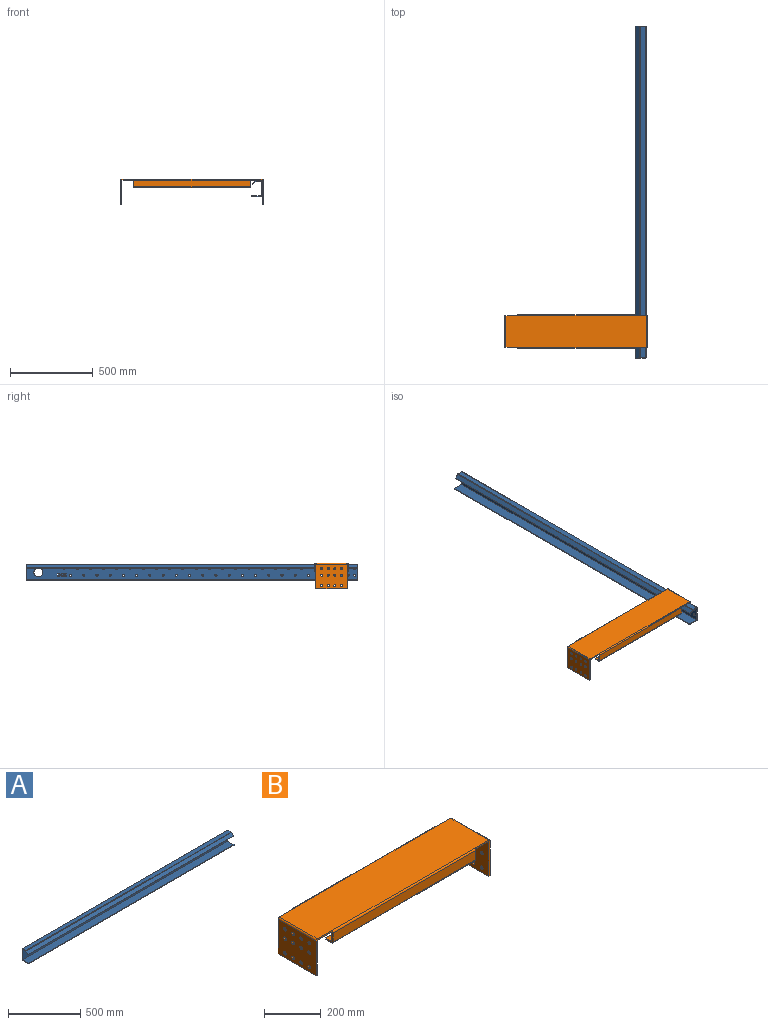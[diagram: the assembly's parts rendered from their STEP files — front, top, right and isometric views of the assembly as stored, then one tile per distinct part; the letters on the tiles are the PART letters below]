
ASSEMBLY  parts=2 mates=1
PART A: 152 faces, bbox 2010x65x99 mm
  f0: plane 59.99x5mm, normal (-1,0,0), area 299.9mm2, adj f2,f3,f4,f149
  f1: plane 59.99x5mm, normal (1,0,0), area 299.9mm2, adj f2,f3,f4,f148
  f2: plane 2010x5mm, normal (0,-1,0), area 10050mm2, adj f0,f1,f3,f4
  f3: plane 2010x59.99mm, normal (0,0,-1), area 120579.9mm2, adj f0,f1,f2,f150
  f4: plane 2010x59.99mm, normal (0,0,1), area 120579.9mm2, adj f0,f1,f2,f151
  f5: plane 5x3.01mm, normal (0,0,-1), area 15.1mm2, adj f6,f128,f129,f130
  f6: plane 9.21x5mm, normal (1,0,0), area 46.1mm2, adj f5,f7,f129,f130
  f7: extruded ~5x2.77mm, area 14.5mm2, adj f6,f8,f129,f130
  f8: extruded ~5x2.04mm, area 13.9mm2, adj f7,f9,f129,f130
  f9: extruded ~5x3.16mm, area 16.2mm2, adj f8,f10,f129,f130
  f10: extruded ~5x4.26mm, area 23mm2, adj f9,f11,f129,f130
  f11: extruded ~5x3.85mm, area 21.3mm2, adj f10,f12,f129,f130
  f12: plane 9.17x5mm, normal (-1,0,0), area 45.9mm2, adj f11,f13,f129,f130
  f13: plane 5x3.01mm, normal (0,0,-1), area 15mm2, adj f12,f14,f129,f130
  f14: plane 8.72x5mm, normal (1,0,0), area 43.6mm2, adj f13,f15,f129,f130
  f15: extruded ~5x2.42mm, area 12.8mm2, adj f14,f16,f129,f130
  f16: extruded ~5x2.19mm, area 12mm2, adj f15,f17,f129,f130
  f17: extruded ~5x2.15mm, area 11.8mm2, adj f16,f18,f129,f130
  f18: extruded ~5x2.43mm, area 12.9mm2, adj f17,f128,f129,f130
  f19: plane 5x2.49mm, normal (-1,0,0), area 12.5mm2, adj f20,f127,f129,f130
  f20: plane 10.22x5mm, normal (0,0,-1), area 51.1mm2, adj f19,f21,f129,f130
  f21: plane 5x1.95mm, normal (1,0,0), area 9.7mm2, adj f20,f22,f129,f130
  f22: plane 9.8x6.82mm, normal (0.82,0,0.57), area 59.7mm2, adj f21,f23,f129,f130
  f23: plane 7x5mm, normal (0,0,-1), area 35mm2, adj f22,f24,f129,f130
  f24: plane 5x2.49mm, normal (1,0,0), area 12.5mm2, adj f23,f25,f129,f130
  f25: plane 10.59x5mm, normal (0,0,1), area 53mm2, adj f24,f26,f129,f130
  f26: plane 5x1.96mm, normal (-1,0,0), area 9.8mm2, adj f25,f27,f129,f130
  f27: plane 9.79x6.83mm, normal (-0.82,0,-0.57), area 59.7mm2, adj f26,f127,f129,f130
  f28: plane 5x3.01mm, normal (0,0,-1), area 15.1mm2, adj f29,f126,f129,f130
  f29: plane 9.21x5mm, normal (1,0,0), area 46.1mm2, adj f28,f30,f129,f130
  f30: extruded ~5x2.77mm, area 14.5mm2, adj f29,f31,f129,f130
  f31: extruded ~5x2.04mm, area 13.9mm2, adj f30,f32,f129,f130
  f32: extruded ~5x3.16mm, area 16.2mm2, adj f31,f33,f129,f130
  f33: extruded ~5x4.26mm, area 23mm2, adj f32,f34,f129,f130
  f34: extruded ~5x3.85mm, area 21.3mm2, adj f33,f35,f129,f130
  f35: plane 9.17x5mm, normal (-1,0,0), area 45.9mm2, adj f34,f36,f129,f130
  f36: plane 5x3.01mm, normal (0,0,-1), area 15mm2, adj f35,f37,f129,f130
  f37: plane 8.72x5mm, normal (1,0,0), area 43.6mm2, adj f36,f38,f129,f130
  f38: extruded ~5x2.42mm, area 12.8mm2, adj f37,f39,f129,f130
  f39: extruded ~5x2.19mm, area 12mm2, adj f38,f40,f129,f130
  f40: extruded ~5x2.15mm, area 11.8mm2, adj f39,f41,f129,f130
  f41: extruded ~5x2.43mm, area 12.9mm2, adj f40,f126,f129,f130
  f42: extruded ~5x2.44mm, area 13mm2, adj f43,f125,f129,f130
  f43: extruded ~5x1.83mm, area 9.3mm2, adj f42,f44,f129,f130
  f44: extruded ~5x1.52mm, area 8mm2, adj f43,f45,f129,f130
  f45: extruded ~5x1.13mm, area 6.5mm2, adj f44,f46,f129,f130
  f46: extruded ~5x0.74mm, area 4mm2, adj f45,f47,f129,f130
  f47: extruded ~5x0.69mm, area 4.7mm2, adj f46,f48,f129,f130
  f48: extruded ~5x1.85mm, area 10.4mm2, adj f47,f49,f129,f130
  f49: extruded ~5x1.32mm, area 7.5mm2, adj f48,f50,f129,f130
  f50: extruded ~5x0.63mm, area 3.9mm2, adj f49,f51,f129,f130
  f51: extruded ~5x1.32mm, area 8.4mm2, adj f50,f52,f129,f130
  f52: extruded ~5x1.75mm, area 9.1mm2, adj f51,f53,f129,f130
  f53: extruded ~5x2.97mm, area 16.7mm2, adj f52,f54,f129,f130
  f54: extruded ~5x3.54mm, area 18.9mm2, adj f53,f55,f129,f130
  f55: extruded ~5x2.12mm, area 10.7mm2, adj f54,f56,f129,f130
  f56: extruded ~5x1.91mm, area 10.1mm2, adj f55,f57,f129,f130
  f57: extruded ~5x0.2mm, area 1.1mm2, adj f56,f58,f129,f130
  f58: plane 5x2.35mm, normal (0.92,0,0.38), area 12.7mm2, adj f57,f59,f129,f130
  f59: extruded ~5x1.89mm, area 10mm2, adj f58,f60,f129,f130
  f60: extruded ~5x1.46mm, area 7.4mm2, adj f59,f61,f129,f130
  f61: extruded ~5x1.32mm, area 7mm2, adj f60,f62,f129,f130
  f62: extruded ~5x1.04mm, area 5.9mm2, adj f61,f63,f129,f130
  f63: extruded ~5x0.7mm, area 3.7mm2, adj f62,f64,f129,f130
  f64: extruded ~5x0.59mm, area 4.1mm2, adj f63,f65,f129,f130
  f65: extruded ~5x1.91mm, area 10.8mm2, adj f64,f66,f129,f130
  f66: extruded ~5x2.2mm, area 13mm2, adj f65,f67,f129,f130
  f67: extruded ~5x0.55mm, area 3.8mm2, adj f66,f68,f129,f130
  f68: extruded ~5x2.35mm, area 12.6mm2, adj f67,f69,f129,f130
  f69: extruded ~5x3.04mm, area 17.3mm2, adj f68,f70,f129,f130
  f70: extruded ~5x3.86mm, area 20.5mm2, adj f69,f71,f129,f130
  f71: extruded ~5x4.03mm, area 20.8mm2, adj f70,f125,f129,f130
  f72: plane 14.24x5mm, normal (1,0,0), area 71.2mm2, adj f73,f124,f129,f130
  f73: plane 5x3.02mm, normal (0,0,1), area 15.1mm2, adj f72,f74,f129,f130
  f74: plane 14.24x5mm, normal (-1,0,0), area 71.2mm2, adj f73,f124,f129,f130
  f75: plane 88.98x5mm, normal (-1,0,0), area 444.9mm2, adj f129,f130,f145,f149
  f76: plane 88.98x5mm, normal (1,0,0), area 444.9mm2, adj f129,f130,f144,f148
  f77: cylinder r=6.5mm len=13mm, axis (0,1,0), area 204.2mm2, adj f129,f130
  f78: cylinder r=6.5mm len=13mm, axis (0,1,0), area 204.2mm2, adj f129,f130
  f79: cylinder r=6.5mm len=13mm, axis (0,1,0), area 204.2mm2, adj f129,f130
  f80: cylinder r=6.5mm len=13mm, axis (0,1,0), area 204.2mm2, adj f129,f130
  f81: cylinder r=6.5mm len=13mm, axis (0,1,0), area 204.2mm2, adj f129,f130
  f82: cylinder r=6.5mm len=13mm, axis (0,1,0), area 204.2mm2, adj f129,f130
  f83: cylinder r=6.5mm len=13mm, axis (0,1,0), area 204.2mm2, adj f129,f130
  f84: cylinder r=6.5mm len=13mm, axis (0,1,0), area 204.2mm2, adj f129,f130
  f85: cylinder r=6.5mm len=13mm, axis (0,1,0), area 204.2mm2, adj f129,f130
  f86: cylinder r=6.5mm len=13mm, axis (0,1,0), area 204.2mm2, adj f129,f130
  f87: cylinder r=6.5mm len=13mm, axis (0,1,0), area 204.2mm2, adj f129,f130
  f88: cylinder r=6.5mm len=13mm, axis (0,1,0), area 204.2mm2, adj f129,f130
  f89: cylinder r=6.5mm len=13mm, axis (0,1,0), area 204.2mm2, adj f129,f130
  f90: cylinder r=6.5mm len=13mm, axis (0,1,0), area 204.2mm2, adj f129,f130
  f91: cylinder r=6.5mm len=13mm, axis (0,1,0), area 204.2mm2, adj f129,f130
  f92: cylinder r=6.5mm len=13mm, axis (0,1,0), area 204.2mm2, adj f129,f130
  f93: cylinder r=6.5mm len=13mm, axis (0,1,0), area 204.2mm2, adj f129,f130
  f94: cylinder r=6.5mm len=13mm, axis (0,1,0), area 204.2mm2, adj f129,f130
  f95: cylinder r=6.5mm len=13mm, axis (0,1,0), area 204.2mm2, adj f129,f130
  f96: cylinder r=6.5mm len=13mm, axis (0,1,0), area 204.2mm2, adj f129,f130
  f97: cylinder r=6.5mm len=13mm, axis (0,1,0), area 204.2mm2, adj f129,f130
  f98: cylinder r=6.5mm len=13mm, axis (0,1,0), area 204.2mm2, adj f129,f130
  f99: cylinder r=6.5mm len=13mm, axis (0,1,0), area 204.2mm2, adj f129,f130
  f100: cylinder r=6.5mm len=13mm, axis (0,1,0), area 204.2mm2, adj f129,f130
  f101: cylinder r=6.5mm len=13mm, axis (0,1,0), area 204.2mm2, adj f129,f130
  f102: cylinder r=6.5mm len=13mm, axis (0,1,0), area 204.2mm2, adj f129,f130
  f103: cylinder r=6.5mm len=13mm, axis (0,1,0), area 204.2mm2, adj f129,f130
  f104: cylinder r=6.5mm len=13mm, axis (0,1,0), area 204.2mm2, adj f129,f130
  f105: cylinder r=6.5mm len=13mm, axis (0,1,0), area 204.2mm2, adj f129,f130
  f106: cylinder r=6.5mm len=13mm, axis (0,1,0), area 204.2mm2, adj f129,f130
  f107: cylinder r=6.5mm len=13mm, axis (0,1,0), area 204.2mm2, adj f129,f130
  f108: cylinder r=6.5mm len=13mm, axis (0,1,0), area 204.2mm2, adj f129,f130
  f109: cylinder r=6.5mm len=13mm, axis (0,1,0), area 204.2mm2, adj f129,f130
  f110: cylinder r=6.5mm len=13mm, axis (0,1,0), area 204.2mm2, adj f129,f130
  f111: cylinder r=6.5mm len=13mm, axis (0,1,0), area 204.2mm2, adj f129,f130
  f112: cylinder r=6.5mm len=13mm, axis (0,1,0), area 204.2mm2, adj f129,f130
  f113: cylinder r=6.5mm len=13mm, axis (0,1,0), area 204.2mm2, adj f129,f130
  f114: cylinder r=6.5mm len=13mm, axis (0,1,0), area 204.2mm2, adj f129,f130
  f115: cylinder r=6.5mm len=13mm, axis (0,1,0), area 204.2mm2, adj f129,f130
  f116: cylinder r=6.5mm len=13mm, axis (0,1,0), area 204.2mm2, adj f129,f130
  f117: cylinder r=27mm len=54mm, axis (0,1,0), area 848.2mm2, adj f129,f130
  f118: cylinder r=6.5mm len=13mm, axis (0,1,0), area 204.2mm2, adj f129,f130
  f119: cylinder r=6.5mm len=13mm, axis (0,1,0), area 204.2mm2, adj f129,f130
  f120: cylinder r=6.5mm len=13mm, axis (0,1,0), area 204.2mm2, adj f129,f130
  f121: cylinder r=6.5mm len=13mm, axis (0,1,0), area 204.2mm2, adj f129,f130
  f122: cylinder r=6.5mm len=13mm, axis (0,1,0), area 204.2mm2, adj f129,f130
  f123: cylinder r=6.5mm len=13mm, axis (0,1,0), area 204.2mm2, adj f129,f130
  f124: plane 5x3.02mm, normal (0,0,-1), area 15.1mm2, adj f72,f74,f129,f130
  f125: plane 5x2.8mm, normal (-1,0,0), area 14mm2, adj f42,f71,f129,f130
  f126: plane 8.7x5mm, normal (-1,0,0), area 43.5mm2, adj f28,f41,f129,f130
  f127: plane 6.64x5mm, normal (0,0,1), area 33.2mm2, adj f19,f27,f129,f130
  f128: plane 8.7x5mm, normal (-1,0,0), area 43.5mm2, adj f5,f18,f129,f130
  f129: plane 2010x88.98mm, normal (0,1,0), area 170067.6mm2, adj f5,f6,f7,f8,f9,f10,f11,f12
  f130: plane 2010x88.98mm, normal (0,-1,0), area 170067.6mm2, adj f5,f6,f7,f8,f9,f10,f11,f12
  f131: plane 31.99x5mm, normal (-1,0,0), area 159.9mm2, adj f133,f134,f141,f145
  f132: plane 31.99x5mm, normal (1,0,0), area 159.9mm2, adj f133,f134,f140,f144
  f133: plane 2010x31.99mm, normal (0,0,1), area 64292mm2, adj f131,f132,f142,f146
  f134: plane 2010x31.99mm, normal (0,0,-1), area 64292mm2, adj f131,f132,f143,f147
  f135: plane 23.87x22.77mm, normal (-1,0,0), area 140mm2, adj f136,f138,f139,f141
  f136: plane 2010x3.65mm, normal (0,-0.73,-0.68), area 10050mm2, adj f135,f137,f138,f139
  f137: plane 23.87x22.77mm, normal (1,0,0), area 140mm2, adj f136,f138,f139,f140
  f138: plane 2010x20.46mm, normal (0,-0.68,0.73), area 56272.1mm2, adj f135,f136,f137,f142
  f139: plane 2010x20.46mm, normal (0,0.68,-0.73), area 56272.1mm2, adj f135,f136,f137,f143
  f140: plane 5x3.42mm, normal (1,0,0), area 9.4mm2, adj f132,f137,f142,f143
  f141: plane 5x3.42mm, normal (-1,0,0), area 9.4mm2, adj f131,f135,f142,f143
  f142: cylinder r=5.01mm len=2010mm, axis (1,0,0), area 7567.5mm2, adj f133,f138,f140,f141
  f143: cylinder r=0.01mm len=2010mm, axis (1,0,0), area 15.1mm2, adj f134,f139,f140,f141
  f144: plane 5.01x5.01mm, normal (1,0,0), area 19.7mm2, adj f76,f132,f146,f147
  f145: plane 5.01x5.01mm, normal (-1,0,0), area 19.7mm2, adj f75,f131,f146,f147
  f146: cylinder r=5.01mm len=2010mm, axis (1,0,0), area 15818.1mm2, adj f129,f133,f144,f145
  f147: cylinder r=0.01mm len=2010mm, axis (1,0,0), area 31.6mm2, adj f130,f134,f144,f145
  f148: plane 5.01x5.01mm, normal (1,0,0), area 19.7mm2, adj f1,f76,f150,f151
  f149: plane 5.01x5.01mm, normal (-1,0,0), area 19.7mm2, adj f0,f75,f150,f151
  f150: cylinder r=5.01mm len=2010mm, axis (1,0,0), area 15818.1mm2, adj f3,f129,f148,f149
  f151: cylinder r=0.01mm len=2010mm, axis (1,0,0), area 31.6mm2, adj f4,f130,f148,f149
PART B: 94 faces, bbox 862x202x156 mm
  f0: plane 70x6mm, normal (0,1,0), area 420mm2, adj f10,f12,f13,f90
  f1: plane 70x6mm, normal (0,-1,0), area 420mm2, adj f7,f12,f13,f73
  f2: plane 6x2.31mm, normal (-1,0,0), area 13.9mm2, adj f8,f12,f13,f56
  f3: plane 6x2.31mm, normal (1,0,0), area 13.9mm2, adj f11,f12,f13,f33
  f4: plane 6x2.31mm, normal (-1,0,0), area 13.9mm2, adj f7,f12,f13,f57
  f5: plane 6x2.31mm, normal (1,0,0), area 13.9mm2, adj f10,f12,f13,f34
  f6: plane 70x6mm, normal (0,-1,0), area 420mm2, adj f11,f12,f13,f74
  f7: plane 6x0.99mm, normal (0,-1,0), area 5.9mm2, adj f1,f4,f12,f13
  f8: plane 6x0.99mm, normal (0,1,0), area 5.9mm2, adj f2,f9,f12,f13
  f9: plane 70x6mm, normal (0,1,0), area 420mm2, adj f8,f12,f13,f91
  f10: plane 6x0.99mm, normal (0,1,0), area 5.9mm2, adj f0,f5,f12,f13
  f11: plane 6x0.99mm, normal (0,-1,0), area 5.9mm2, adj f3,f6,f12,f13
  f12: plane 849.98x189.98mm, normal (0,0,-1), area 161479.2mm2, adj f0,f1,f2,f3,f4,f5,f6,f7
  f13: plane 849.98x189.98mm, normal (0,0,1), area 161479.2mm2, adj f0,f1,f2,f3,f4,f5,f6,f7
  f14: plane 6x2.32mm, normal (0,0,1), area 13.9mm2, adj f30,f31,f32,f34
  f15: plane 190x6mm, normal (0,0,-1), area 1140mm2, adj f16,f30,f31,f32
  f16: plane 149.99x6mm, normal (0,-1,0), area 899.9mm2, adj f15,f17,f31,f32
  f17: plane 6x2.32mm, normal (0,0,1), area 13.9mm2, adj f16,f31,f32,f33
  f18: cylinder r=6.5mm len=13mm, axis (-1,0,0), area 245mm2, adj f31,f32
  f19: cylinder r=6.5mm len=13mm, axis (-1,0,0), area 245mm2, adj f31,f32
  f20: cylinder r=6.5mm len=13mm, axis (-1,0,0), area 245mm2, adj f31,f32
  f21: cylinder r=6.5mm len=13mm, axis (-1,0,0), area 245mm2, adj f31,f32
  f22: cylinder r=6.5mm len=13mm, axis (-1,0,0), area 245mm2, adj f31,f32
  f23: cylinder r=6.5mm len=13mm, axis (-1,0,0), area 245mm2, adj f31,f32
  f24: cylinder r=6.5mm len=13mm, axis (-1,0,0), area 245mm2, adj f31,f32
  f25: cylinder r=6.5mm len=13mm, axis (-1,0,0), area 245mm2, adj f31,f32
  f26: cylinder r=6.5mm len=13mm, axis (-1,0,0), area 245mm2, adj f31,f32
  f27: cylinder r=6.5mm len=13mm, axis (-1,0,0), area 245mm2, adj f31,f32
  f28: cylinder r=6.5mm len=13mm, axis (-1,0,0), area 245mm2, adj f31,f32
  f29: cylinder r=6.5mm len=13mm, axis (-1,0,0), area 245mm2, adj f31,f32
  f30: plane 149.99x6mm, normal (0,1,0), area 899.9mm2, adj f14,f15,f31,f32
  f31: plane 190x149.99mm, normal (-1,0,0), area 26905.3mm2, adj f14,f15,f16,f17,f18,f19,f20,f21
  f32: plane 190x149.99mm, normal (1,0,0), area 26905.3mm2, adj f14,f15,f16,f17,f18,f19,f20,f21
  f33: plane 6.01x6.01mm, normal (0,-1,0), area 28.4mm2, adj f3,f17,f35,f36
  f34: plane 6.01x6.01mm, normal (0,1,0), area 28.4mm2, adj f5,f14,f35,f36
  f35: cylinder r=6.01mm len=185.36mm, axis (0,-1,0), area 1749.9mm2, adj f13,f32,f33,f34
  f36: cylinder r=0.01mm len=185.36mm, axis (0,-1,0), area 2.9mm2, adj f12,f31,f33,f34
  f37: plane 6x2.32mm, normal (0,0,1), area 13.9mm2, adj f53,f54,f55,f57
  f38: plane 190x6mm, normal (0,0,-1), area 1140mm2, adj f39,f53,f54,f55
  f39: plane 149.99x6mm, normal (0,1,0), area 899.9mm2, adj f38,f40,f54,f55
  f40: plane 6x2.32mm, normal (0,0,1), area 13.9mm2, adj f39,f54,f55,f56
  f41: cylinder r=6.5mm len=13mm, axis (1,0,0), area 245mm2, adj f54,f55
  f42: cylinder r=6.5mm len=13mm, axis (1,0,0), area 245mm2, adj f54,f55
  f43: cylinder r=6.5mm len=13mm, axis (1,0,0), area 245mm2, adj f54,f55
  f44: cylinder r=6.5mm len=13mm, axis (1,0,0), area 245mm2, adj f54,f55
  f45: cylinder r=6.5mm len=13mm, axis (1,0,0), area 245mm2, adj f54,f55
  f46: cylinder r=6.5mm len=13mm, axis (1,0,0), area 245mm2, adj f54,f55
  f47: cylinder r=6.5mm len=13mm, axis (1,0,0), area 245mm2, adj f54,f55
  f48: cylinder r=6.5mm len=13mm, axis (1,0,0), area 245mm2, adj f54,f55
  f49: cylinder r=6.5mm len=13mm, axis (1,0,0), area 245mm2, adj f54,f55
  f50: cylinder r=6.5mm len=13mm, axis (1,0,0), area 245mm2, adj f54,f55
  f51: cylinder r=6.5mm len=13mm, axis (1,0,0), area 245mm2, adj f54,f55
  f52: cylinder r=6.5mm len=13mm, axis (1,0,0), area 245mm2, adj f54,f55
  f53: plane 149.99x6mm, normal (0,-1,0), area 899.9mm2, adj f37,f38,f54,f55
  f54: plane 190x149.99mm, normal (1,0,0), area 26905.3mm2, adj f37,f38,f39,f40,f41,f42,f43,f44
  f55: plane 190x149.99mm, normal (-1,0,0), area 26905.3mm2, adj f37,f38,f39,f40,f41,f42,f43,f44
  f56: plane 6.01x6.01mm, normal (0,1,0), area 28.4mm2, adj f2,f40,f58,f59
  f57: plane 6.01x6.01mm, normal (0,-1,0), area 28.4mm2, adj f4,f37,f58,f59
  f58: cylinder r=6.01mm len=185.36mm, axis (0,1,0), area 1749.9mm2, adj f13,f55,f56,f57
  f59: cylinder r=0.01mm len=185.36mm, axis (0,1,0), area 2.9mm2, adj f12,f54,f56,f57
  f60: plane 708x6mm, normal (0,1,0), area 4248mm2, adj f61,f62,f63,f64
  f61: plane 29.99x6mm, normal (-1,0,0), area 179.9mm2, adj f60,f63,f64,f65
  f62: plane 29.99x6mm, normal (1,0,0), area 179.9mm2, adj f60,f63,f64,f66
  f63: plane 708x29.99mm, normal (0,0,1), area 21232.9mm2, adj f60,f61,f62,f68
  f64: plane 708x29.99mm, normal (0,0,-1), area 21232.9mm2, adj f60,f61,f62,f67
  f65: plane 6.01x6.01mm, normal (-1,0,0), area 28.4mm2, adj f61,f67,f68,f70
  f66: plane 6.01x6.01mm, normal (1,0,0), area 28.4mm2, adj f62,f67,f68,f69
  f67: cylinder r=6.01mm len=708mm, axis (-1,0,0), area 6683.9mm2, adj f64,f65,f66,f72
  f68: cylinder r=0.01mm len=708mm, axis (-1,0,0), area 11.1mm2, adj f63,f65,f66,f71
  f69: plane 39.98x6mm, normal (1,0,0), area 239.9mm2, adj f66,f71,f72,f74
  f70: plane 39.98x6mm, normal (-1,0,0), area 239.9mm2, adj f65,f71,f72,f73
  f71: plane 708x39.98mm, normal (0,1,0), area 28305.8mm2, adj f68,f69,f70,f76
  f72: plane 708x39.98mm, normal (0,-1,0), area 28305.8mm2, adj f67,f69,f70,f75
  f73: plane 6.01x6.01mm, normal (-1,0,0), area 28.4mm2, adj f1,f70,f75,f76
  f74: plane 6.01x6.01mm, normal (1,0,0), area 28.4mm2, adj f6,f69,f75,f76
  f75: cylinder r=6.01mm len=708mm, axis (-1,0,0), area 6683.9mm2, adj f13,f72,f73,f74
  f76: cylinder r=0.01mm len=708mm, axis (-1,0,0), area 11.1mm2, adj f12,f71,f73,f74
  f77: plane 708x6mm, normal (0,-1,0), area 4248mm2, adj f78,f79,f80,f81
  f78: plane 29.99x6mm, normal (1,0,0), area 179.9mm2, adj f77,f80,f81,f82
  f79: plane 29.99x6mm, normal (-1,0,0), area 179.9mm2, adj f77,f80,f81,f83
  f80: plane 708x29.99mm, normal (0,0,1), area 21232.9mm2, adj f77,f78,f79,f85
  f81: plane 708x29.99mm, normal (0,0,-1), area 21232.9mm2, adj f77,f78,f79,f84
  f82: plane 6.01x6.01mm, normal (1,0,0), area 28.4mm2, adj f78,f84,f85,f87
  f83: plane 6.01x6.01mm, normal (-1,0,0), area 28.4mm2, adj f79,f84,f85,f86
  f84: cylinder r=6.01mm len=708mm, axis (1,0,0), area 6683.9mm2, adj f81,f82,f83,f89
  f85: cylinder r=0.01mm len=708mm, axis (1,0,0), area 11.1mm2, adj f80,f82,f83,f88
  f86: plane 39.98x6mm, normal (-1,0,0), area 239.9mm2, adj f83,f88,f89,f91
  f87: plane 39.98x6mm, normal (1,0,0), area 239.9mm2, adj f82,f88,f89,f90
  f88: plane 708x39.98mm, normal (0,-1,0), area 28305.8mm2, adj f85,f86,f87,f93
  f89: plane 708x39.98mm, normal (0,1,0), area 28305.8mm2, adj f84,f86,f87,f92
  f90: plane 6.01x6.01mm, normal (1,0,0), area 28.4mm2, adj f0,f87,f92,f93
  f91: plane 6.01x6.01mm, normal (-1,0,0), area 28.4mm2, adj f9,f86,f92,f93
  f92: cylinder r=6.01mm len=708mm, axis (1,0,0), area 6683.9mm2, adj f13,f89,f90,f91
  f93: cylinder r=0.01mm len=708mm, axis (1,0,0), area 11.1mm2, adj f12,f88,f90,f91
PLACE A rot(axis=(0,0,-1),90deg) t=(715.21,1979.36,-87.14)mm
PLACE B t=(-129.79,34.36,13.38)mm
MATE fastened A.f119 <-> B.f46  axis (1,0,0) through (720.21,69.36,-19.63)mm
